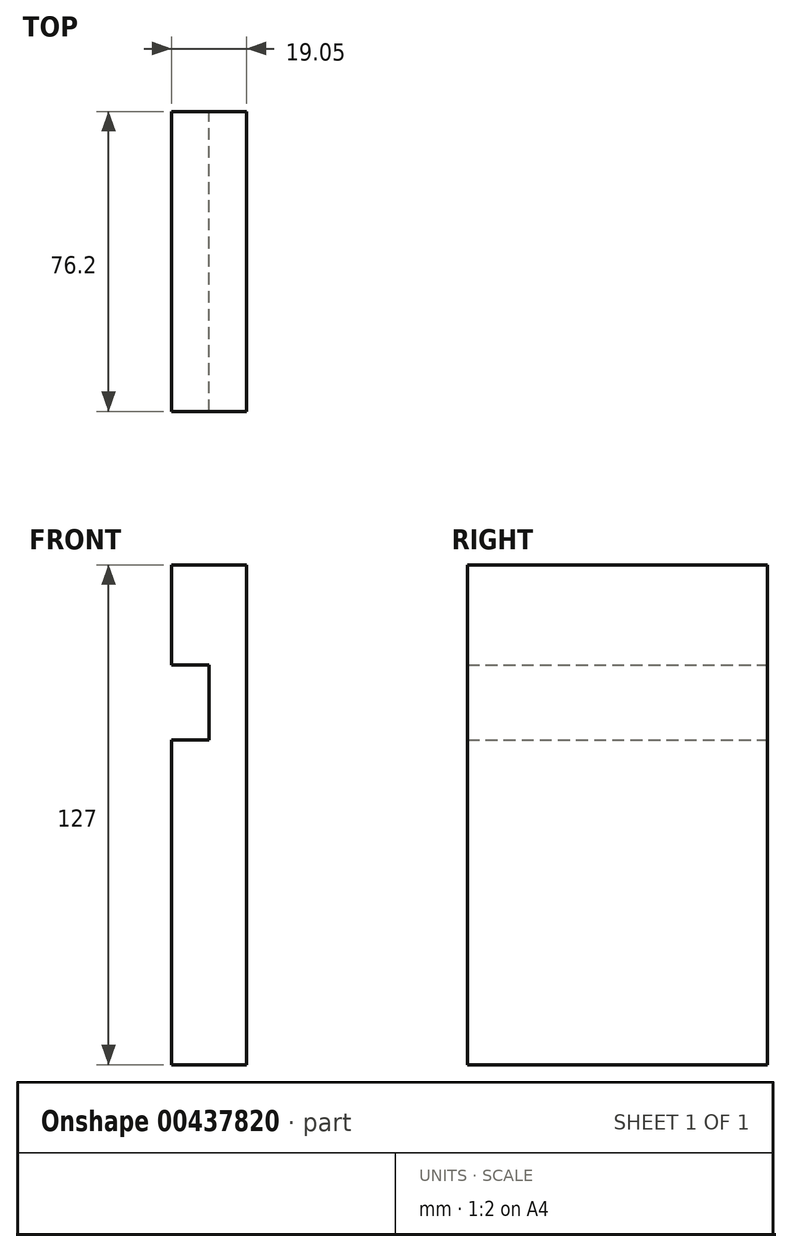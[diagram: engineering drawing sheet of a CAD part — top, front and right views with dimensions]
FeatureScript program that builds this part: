
annotation { "Feature Type Name" : "Feature", "Feature Type Description" : "" }
export const myFeature = defineFeature(function(context is Context, id is Id, definition is map)
    precondition{}
    {
        {
            var Q0;
            Q0=qCreatedBy(makeId("Front.planeOp"),FACE);
            var sketch = newSketch(context, id + "F0", { "sketchPlane" : qUnion([Q0])});
            skLineSegment(sketch, "E0", {"start": v(0, -68.76) * mm, "end": v(0, 58.24) * mm});
            skLineSegment(sketch, "E1", {"start": v(0, 58.24) * mm, "end": v(-19.05, 58.24) * mm});
            skLineSegment(sketch, "E2", {"start": v(-19.05, 58.24) * mm, "end": v(-19.05, 32.84) * mm});
            skLineSegment(sketch, "E3", {"start": v(-19.05, 32.84) * mm, "end": v(-9.53, 32.84) * mm});
            skLineSegment(sketch, "E4", {"start": v(-9.53, 32.84) * mm, "end": v(-9.53, 13.79) * mm});
            skLineSegment(sketch, "E5", {"start": v(-9.53, 13.79) * mm, "end": v(-19.05, 13.79) * mm});
            skLineSegment(sketch, "E6", {"start": v(0, -68.76) * mm, "end": v(-19.05, -68.76) * mm});
            skLineSegment(sketch, "E7", {"start": v(-19.05, -68.76) * mm, "end": v(-19.05, 13.79) * mm});
            skSolve(sketch);
        }
        {
            var Q0;
            Q0 = qSketchRegion(id + "F0", true);
            extrude(context, id + "F1", {"entities" : qUnion([Q0]), "depth" : 76.2 * mm});
        }
    });
